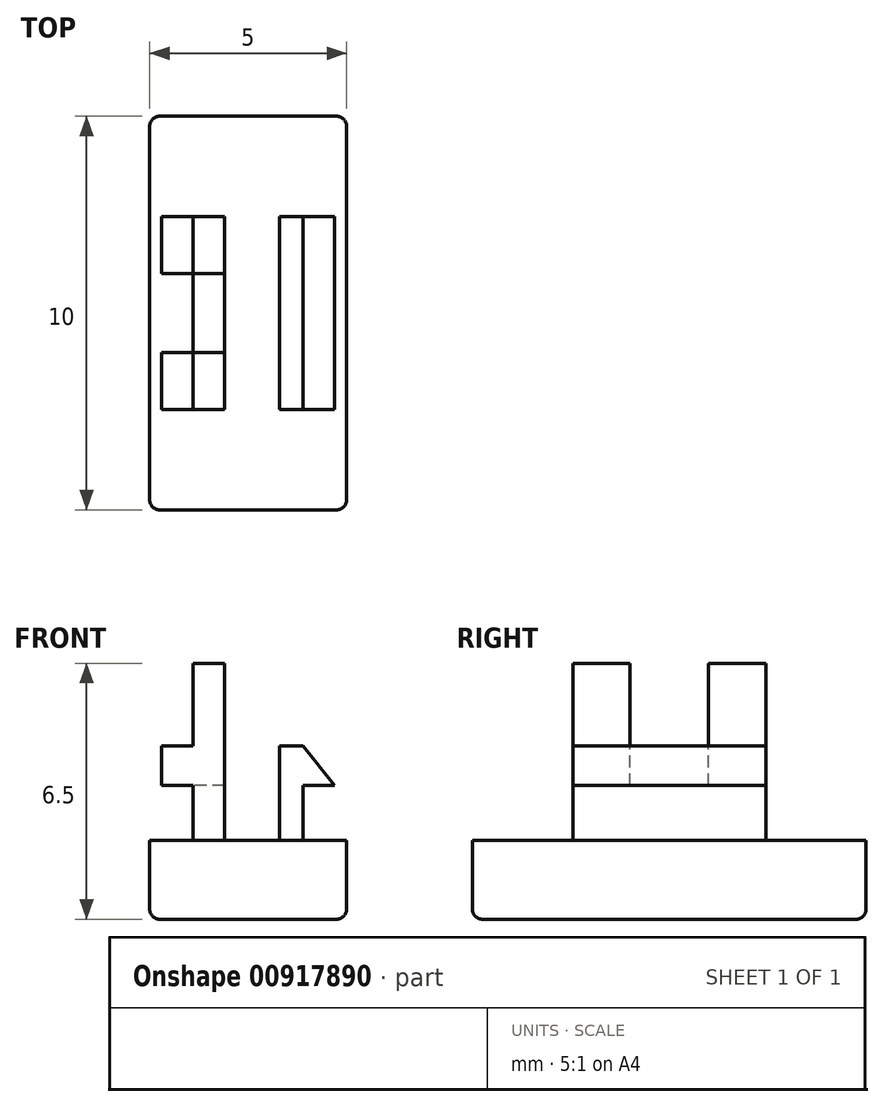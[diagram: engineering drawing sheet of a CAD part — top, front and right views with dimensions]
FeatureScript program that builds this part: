
annotation { "Feature Type Name" : "Feature", "Feature Type Description" : "" }
export const myFeature = defineFeature(function(context is Context, id is Id, definition is map)
    precondition{}
    {
        {
            var Q0;
            Q0=qCreatedBy(makeId("Top.planeOp"),FACE);
            var sketch = newSketch(context, id + "F0", { "sketchPlane" : qUnion([Q0])});
            skLineSegment(sketch, "E0.top", {"start": v(-2.5, 5) * mm, "end": v(2.5, 5) * mm});
            skLineSegment(sketch, "E0.right", {"start": v(2.5, -5) * mm, "end": v(2.5, 5) * mm});
            skLineSegment(sketch, "E1", {"start": v(-2.5, 5) * mm, "end": v(-2.5, -5) * mm});
            skLineSegment(sketch, "E2", {"start": v(-2.5, -5) * mm, "end": v(2.5, -5) * mm});
            skSolve(sketch);
        }
        {
            var Q0;
            Q0=makeQuery(id+"F0.imprint","IMPRINT",FACE,{"disambiguationData":[TD([[makeQuery(id+"F0.imprint","IMPRINT",EDGE,{"derivedFrom":sQuery(id+"F0.wireOp",EDGE,"E0.top")}),-1.0]])]});
            extrude(context, id + "F1", {"entities" : qUnion([Q0]), "depth" : 2 * mm, "offsetDistance" : 25 * mm});
        }
        {
            var Q0;
            Q0=makeQuery(id+"F1.opExtrude","SWEPT_EDGE",EDGE,{"disambiguationData":[OSD([sQuery(id+"F0.wireOp",EDGE,"E0.bottom"),sQuery(id+"F0.wireOp",EDGE,"E0.right")])]});
            var Q1;
            Q1=makeQuery(id+"F1.opExtrude","SWEPT_EDGE",EDGE,{"disambiguationData":[OSD([sQuery(id+"F0.wireOp",EDGE,"E0.top"),sQuery(id+"F0.wireOp",EDGE,"E0.right")])]});
            var Q2;
            Q2=makeQuery(id+"F1.opExtrude","SWEPT_EDGE",EDGE,{"disambiguationData":[OSD([sQuery(id+"F0.wireOp",EDGE,"E0.bottom"),sQuery(id+"F0.wireOp",EDGE,"E0.left")])]});
            var Q3;
            Q3=makeQuery(id+"F1.opExtrude","SWEPT_EDGE",EDGE,{"disambiguationData":[OSD([sQuery(id+"F0.wireOp",EDGE,"E0.top"),sQuery(id+"F0.wireOp",EDGE,"E0.left")])]});
            var Q4;
            Q4=makeQuery(id+"F1.opExtrude","SWEPT_EDGE",EDGE,{"disambiguationData":[OSD([sQuery(id+"F0.wireOp",EDGE,"E1"),sQuery(id+"F0.wireOp",EDGE,"E2")])]});
            var Q5;
            Q5=makeQuery(id+"F1.opExtrude","CAP_EDGE",EDGE,{"disambiguationData":[OSD([sQuery(id+"F0.wireOp",EDGE,"E0.top")])],"isStart":true});
            var Q6;
            Q6=makeQuery(id+"F1.opExtrude","CAP_EDGE",EDGE,{"disambiguationData":[OSD([sQuery(id+"F0.wireOp",EDGE,"E0.right")])],"isStart":true});
            var Q7;
            Q7=makeQuery(id+"F1.opExtrude","CAP_EDGE",EDGE,{"disambiguationData":[OSD([sQuery(id+"F0.wireOp",EDGE,"E1")])],"isStart":true});
            var Q8;
            Q8=makeQuery(id+"F1.opExtrude","CAP_EDGE",EDGE,{"disambiguationData":[OSD([sQuery(id+"F0.wireOp",EDGE,"E2")])],"isStart":true});
            fillet(context, id + "F2", {"entities" : qUnion([Q0, Q1, Q2, Q3, Q4, Q5, Q6, Q7, Q8]), "radius" : 0.25 * mm, "tangentPropagation" : true, "allowEdgeOverflow" : false});
        }
        {
            var Q0;
            Q0=qCreatedBy(makeId("Front.planeOp"),FACE);
            var sketch = newSketch(context, id + "F3", { "sketchPlane" : qUnion([Q0])});
            skLineSegment(sketch, "E3", {"start": v(0.8, 2) * mm, "end": v(0.8, 4.4) * mm});
            skLineSegment(sketch, "E4", {"start": v(2.2, 3.4) * mm, "end": v(1.4, 3.4) * mm});
            skLineSegment(sketch, "E5", {"start": v(1.4, 3.4) * mm, "end": v(1.4, 2) * mm});
            skLineSegment(sketch, "E6", {"start": v(0.8, 2) * mm, "end": v(1.4, 2) * mm});
            skLineSegment(sketch, "E7", {"start": v(2.2, 3.4) * mm, "end": v(1.4, 4.4) * mm});
            skLineSegment(sketch, "E8", {"start": v(1.4, 4.4) * mm, "end": v(0.8, 4.4) * mm});
            skSolve(sketch);
        }
        {
            var Q0;
            Q0=makeQuery(id+"F3.imprint","IMPRINT",FACE,{"disambiguationData":[TD([[makeQuery(id+"F3.imprint","IMPRINT",EDGE,{"derivedFrom":sQuery(id+"F3.wireOp",EDGE,"E3")}),-1.0]])]});
            extrude(context, id + "F4", {"entities" : qUnion([Q0]), "operationType" : NewBodyOperationType.ADD, "endBound" : BoundingType.SYMMETRIC, "depth" : 4.9 * mm, "offsetDistance" : 25 * mm});
        }
        {
            var Q0;
            Q0=qCreatedBy(makeId("Front.planeOp"),FACE);
            var sketch = newSketch(context, id + "F5", { "sketchPlane" : qUnion([Q0])});
            skLineSegment(sketch, "E9.bottom", {"start": v(-1.4, 2) * mm, "end": v(-0.6, 2) * mm});
            skLineSegment(sketch, "E9.top", {"start": v(-1.4, 6.5) * mm, "end": v(-0.6, 6.5) * mm});
            skLineSegment(sketch, "E9.left", {"start": v(-1.4, 2) * mm, "end": v(-1.4, 6.5) * mm});
            skLineSegment(sketch, "E9.right", {"start": v(-0.6, 2) * mm, "end": v(-0.6, 6.5) * mm});
            skSolve(sketch);
        }
        {
            var Q0;
            Q0=makeQuery(id+"F5.imprint","IMPRINT",FACE,{"disambiguationData":[TD([[makeQuery(id+"F5.imprint","IMPRINT",EDGE,{"derivedFrom":sQuery(id+"F5.wireOp",EDGE,"E9.bottom")}),1.0]])]});
            extrude(context, id + "F6", {"entities" : qUnion([Q0]), "operationType" : NewBodyOperationType.ADD, "endBound" : BoundingType.SYMMETRIC, "depth" : 4.9 * mm, "offsetDistance" : 25 * mm});
        }
        {
            var Q0;
            Q0=makeQuery(id+"F6.opExtrude","SWEPT_FACE",FACE,{"disambiguationData":[OSD([sQuery(id+"F5.wireOp",EDGE,"E9.left")])]});
            var sketch = newSketch(context, id + "F7", { "sketchPlane" : qUnion([Q0])});
            skLineSegment(sketch, "E10.bottom", {"start": v(-1, 6.5) * mm, "end": v(1, 6.5) * mm});
            skLineSegment(sketch, "E10.top", {"start": v(-1, 3.4) * mm, "end": v(1, 3.4) * mm});
            skLineSegment(sketch, "E10.left", {"start": v(-1, 6.5) * mm, "end": v(-1, 3.4) * mm});
            skLineSegment(sketch, "E10.right", {"start": v(1, 6.5) * mm, "end": v(1, 3.4) * mm});
            skSolve(sketch);
        }
        {
            var Q0;
            Q0=makeQuery(id+"F7.imprint","IMPRINT",FACE,{"disambiguationData":[TD([[makeQuery(id+"F7.imprint","IMPRINT",EDGE,{"derivedFrom":sQuery(id+"F7.wireOp",EDGE,"E10.bottom")}),1.0]])]});
            var Q1;
            Q1=makeQuery(id+"F6.opExtrude","SWEPT_FACE",FACE,{"disambiguationData":[OSD([sQuery(id+"F5.wireOp",EDGE,"E9.right")])]});
            extrude(context, id + "F8", {"entities" : qUnion([Q0]), "operationType" : NewBodyOperationType.REMOVE, "endBound" : BoundingType.UP_TO_SURFACE, "oppositeDirection" : true, "depth" : 25 * mm, "endBoundEntityFace" : qUnion([Q1]), "offsetDistance" : 25 * mm});
        }
        {
            var Q0;
            Q0=makeQuery(id+"F6.opExtrude","SWEPT_FACE",FACE,{"disambiguationData":[OSD([sQuery(id+"F5.wireOp",EDGE,"E9.left")])]});
            var sketch = newSketch(context, id + "F9", { "sketchPlane" : qUnion([Q0])});
            skLineSegment(sketch, "E11.bottom", {"start": v(-1, 3.4) * mm, "end": v(-2.45, 3.4) * mm});
            skLineSegment(sketch, "E11.top", {"start": v(-1, 4.4) * mm, "end": v(-2.45, 4.4) * mm});
            skLineSegment(sketch, "E11.left", {"start": v(-1, 3.4) * mm, "end": v(-1, 4.4) * mm});
            skLineSegment(sketch, "E11.right", {"start": v(-2.45, 3.4) * mm, "end": v(-2.45, 4.4) * mm});
            skLineSegment(sketch, "E12.bottom", {"start": v(1, 3.4) * mm, "end": v(2.45, 3.4) * mm});
            skLineSegment(sketch, "E12.top", {"start": v(1, 4.4) * mm, "end": v(2.45, 4.4) * mm});
            skLineSegment(sketch, "E12.left", {"start": v(1, 3.4) * mm, "end": v(1, 4.4) * mm});
            skLineSegment(sketch, "E12.right", {"start": v(2.45, 3.4) * mm, "end": v(2.45, 4.4) * mm});
            skSolve(sketch);
        }
        {
            var Q0;
            Q0=makeQuery(id+"F9.imprint","IMPRINT",FACE,{"disambiguationData":[TD([[makeQuery(id+"F9.imprint","IMPRINT",EDGE,{"derivedFrom":sQuery(id+"F9.wireOp",EDGE,"E11.bottom")}),-1.0]])]});
            var Q1;
            Q1=makeQuery(id+"F9.imprint","IMPRINT",FACE,{"disambiguationData":[TD([[makeQuery(id+"F9.imprint","IMPRINT",EDGE,{"derivedFrom":sQuery(id+"F9.wireOp",EDGE,"E12.bottom")}),1.0]])]});
            extrude(context, id + "F10", {"entities" : qUnion([Q0, Q1]), "operationType" : NewBodyOperationType.ADD, "depth" : 0.8 * mm, "offsetDistance" : 25 * mm});
        }
    });
